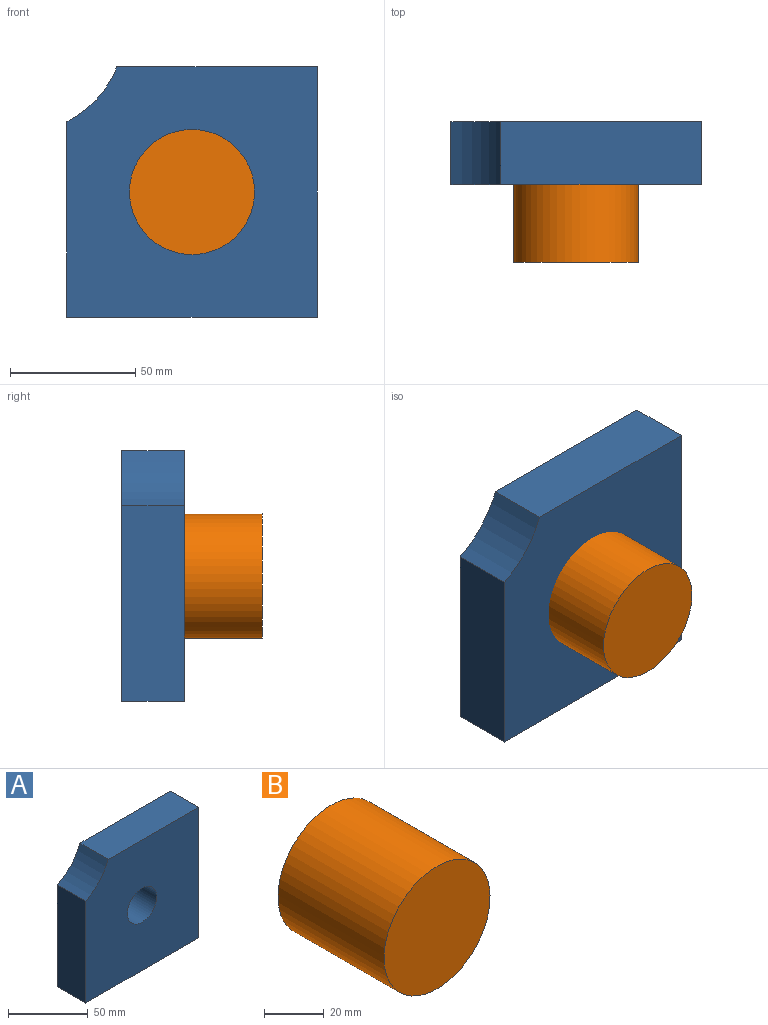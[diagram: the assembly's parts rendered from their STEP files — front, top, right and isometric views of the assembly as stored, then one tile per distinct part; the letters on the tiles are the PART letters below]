
ASSEMBLY  parts=2 mates=1
PART A: 8 faces, bbox 100x25x100 mm
  f0: plane 80x25mm, normal (0,0,1), area 2000.1mm2, adj f4,f5,f6,f7
  f1: plane 78.07x25mm, normal (-1,0,0), area 1951.6mm2, adj f2,f5,f6,f7
  f2: plane 100x25mm, normal (0,0,-1), area 2500mm2, adj f1,f4,f5,f6
  f3: cylinder r=13mm len=26mm, axis (0,1,0), area 2042mm2, adj f5,f6
  f4: plane 100x25mm, normal (1,0,0), area 2500mm2, adj f0,f2,f5,f6
  f5: plane 100x100mm, normal (0,-1,0), area 9194.2mm2, adj f0,f1,f2,f3,f4,f7
  f6: plane 100x100mm, normal (0,1,0), area 9194.2mm2, adj f0,f1,f2,f3,f4,f7
  f7: cylinder r=40.9mm len=25mm, axis (0,-1,0), area 759.4mm2, adj f0,f1,f5,f6
PART B: 3 faces, bbox 50x50x50 mm
  f0: cylinder r=25mm len=50mm, axis (0,1,0), area 7854mm2, adj f1,f2
  f1: plane 50x50mm, normal (0,-1,0), area 1963.5mm2, adj f0
  f2: plane 50x50mm, normal (0,1,0), area 1963.5mm2, adj f0
PLACE A t=(-18.08,-10.44,43.44)mm
PLACE B t=(-18.08,-16.57,43.44)mm
MATE cylindrical A.f3 <-> B.f0  axis (0,1,0) through (-18.08,-35.44,43.44)mm
